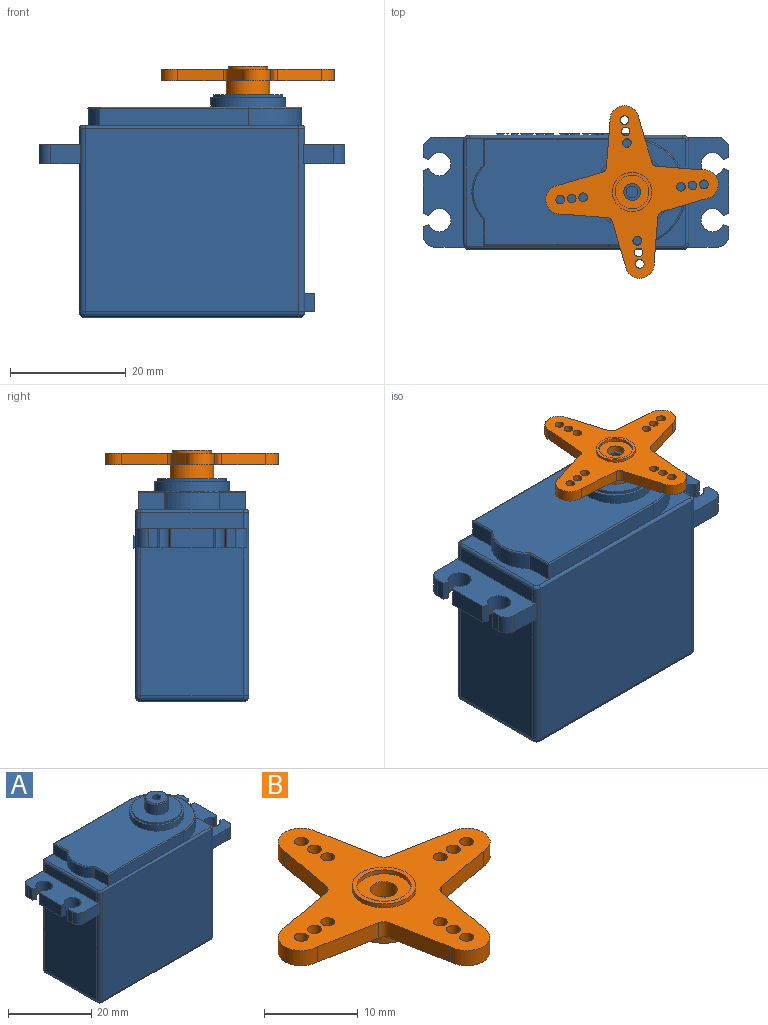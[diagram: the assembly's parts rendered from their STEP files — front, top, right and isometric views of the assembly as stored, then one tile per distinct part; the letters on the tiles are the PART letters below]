
ASSEMBLY  parts=2 mates=1
PART A: 315 faces, bbox 52.9x20.2x41.8 mm
  f0: plane 25.56x17.7mm, normal (1,0,0), area 432.3mm2, adj f18,f38,f39,f40,f310,f311,f313
  f1: plane 37x31.7mm, normal (0,1,0), area 1154.2mm2, adj f40,f45,f46,f67,f85,f86,f87,f88
  f2: plane 38x18.7mm, normal (0,0,1), area 83.6mm2, adj f50,f51,f52,f53,f54,f55,f65,f66
  f3: plane 17.7x2.8mm, normal (1,0,0), area 49.6mm2, adj f17,f38,f40,f71
  f4: plane 17.7x2.8mm, normal (-1,0,0), area 49.6mm2, adj f23,f43,f46,f66
  f5: plane 25.56x17.7mm, normal (-1,0,0), area 452.4mm2, adj f24,f43,f46,f49
  f6: plane 37x17.7mm, normal (0,0,-1), area 654.9mm2, adj f39,f44,f45,f49
  f7: plane 37x31.7mm, normal (0,-1,0), area 1172.9mm2, adj f38,f43,f44,f70
  f8: plane 3.34x1.49mm, normal (1,0,0), area 5mm2, adj f9,f17,f18,f35
  f9: plane 3.34x0.96mm, normal (0.38,0.92,0), area 3.5mm2, adj f8,f10,f17,f18
  f10: cylinder r=2mm len=4mm, axis (0,0,-1), area 36.7mm2, adj f9,f11,f17,f18
  f11: plane 3.34x0.96mm, normal (0.38,-0.92,0), area 3.5mm2, adj f10,f12,f17,f18
  f12: plane 7.38x3.34mm, normal (1,0,0), area 24.6mm2, adj f11,f13,f17,f18
  f13: plane 3.34x0.96mm, normal (0.38,0.92,0), area 3.5mm2, adj f12,f14,f17,f18
  f14: cylinder r=2mm len=4mm, axis (0,0,-1), area 36.7mm2, adj f13,f15,f17,f18
  f15: plane 3.34x0.96mm, normal (0.38,-0.92,0), area 3.5mm2, adj f14,f16,f17,f18
  f16: plane 3.34x1.49mm, normal (1,0,0), area 5mm2, adj f15,f17,f18,f36
  f17: plane 19x7.17mm, normal (0,0,1), area 101.5mm2, adj f3,f8,f9,f10,f11,f12,f13,f14
  f18: plane 19x7.17mm, normal (0,0,-1), area 101.5mm2, adj f0,f8,f9,f10,f11,f12,f13,f14
  f19: plane 5.17x3.34mm, normal (0,1,0), area 17.3mm2, adj f17,f18,f36,f40
  f20: plane 5.17x3.34mm, normal (0,-1,0), area 17.3mm2, adj f17,f18,f35,f38
  f21: plane 5.17x3.34mm, normal (0,-1,0), area 17.3mm2, adj f23,f24,f34,f43
  f22: plane 5.17x3.34mm, normal (0,1,0), area 17.3mm2, adj f23,f24,f37,f46
  f23: plane 19x7.17mm, normal (0,0,1), area 101.5mm2, adj f4,f21,f22,f25,f26,f27,f28,f29
  f24: plane 19x7.17mm, normal (0,0,-1), area 101.5mm2, adj f5,f21,f22,f25,f26,f27,f28,f29
  f25: plane 3.34x0.96mm, normal (-0.38,-0.92,0), area 3.5mm2, adj f23,f24,f26,f33
  f26: cylinder r=2mm len=4mm, axis (0,0,-1), area 36.7mm2, adj f23,f24,f25,f27
  f27: plane 3.34x0.96mm, normal (-0.38,0.92,0), area 3.5mm2, adj f23,f24,f26,f28
  f28: plane 7.38x3.34mm, normal (-1,0,0), area 24.6mm2, adj f23,f24,f27,f29
  f29: plane 3.34x0.96mm, normal (-0.38,-0.92,0), area 3.5mm2, adj f23,f24,f28,f30
  f30: cylinder r=2mm len=4mm, axis (0,0,-1), area 36.7mm2, adj f23,f24,f29,f31
  f31: plane 3.34x0.96mm, normal (-0.38,0.92,0), area 3.5mm2, adj f23,f24,f30,f32
  f32: plane 3.34x1.49mm, normal (-1,0,0), area 5mm2, adj f23,f24,f31,f34
  f33: plane 3.34x1.49mm, normal (-1,0,0), area 5mm2, adj f23,f24,f25,f37
  f34: cylinder r=2mm len=3.34mm, axis (0,0,-1), area 10.5mm2, adj f21,f23,f24,f32
  f35: cylinder r=2mm len=3.34mm, axis (0,0,1), area 10.5mm2, adj f8,f17,f18,f20
  f36: cylinder r=2mm len=3.34mm, axis (0,0,-1), area 10.5mm2, adj f16,f17,f18,f19
  f37: cylinder r=2mm len=3.34mm, axis (0,0,1), area 10.5mm2, adj f22,f23,f24,f33
  f38: cylinder r=1mm len=31.7mm, axis (0,0,-1), area 47.4mm2, adj f0,f3,f7,f17,f18,f20,f41,f72
  f39: cylinder r=1mm len=17.7mm, axis (0,-1,0), area 27.8mm2, adj f0,f6,f41,f42,f312
  f40: cylinder r=1mm len=31.7mm, axis (0,0,1), area 47.4mm2, adj f0,f1,f3,f17,f18,f19,f42,f69
  f41: sphere r=1mm, area 1.6mm2, adj f38,f39,f44
  f42: sphere r=1mm, area 1.6mm2, adj f39,f40,f45
  f43: cylinder r=1mm len=31.7mm, axis (0,0,1), area 47.4mm2, adj f4,f5,f7,f21,f23,f24,f47,f68
  f44: cylinder r=1mm len=37mm, axis (-1,0,0), area 58.1mm2, adj f6,f7,f41,f47
  f45: cylinder r=1mm len=37mm, axis (1,0,0), area 58.1mm2, adj f1,f6,f42,f48
  f46: cylinder r=1mm len=31.7mm, axis (0,0,-1), area 47.4mm2, adj f1,f4,f5,f22,f23,f24,f48,f65
  f47: sphere r=1mm, area 1.6mm2, adj f43,f44,f49
  f48: sphere r=1mm, area 1.6mm2, adj f45,f46,f49
  f49: cylinder r=1mm len=17.7mm, axis (0,1,0), area 27.8mm2, adj f5,f6,f47,f48
  f50: plane 25.7x2.95mm, normal (0,-1,0), area 75.8mm2, adj f2,f51,f55,f61
  f51: cylinder r=9.3mm len=18.6mm, axis (0,0,-1), area 86.2mm2, adj f2,f50,f52,f59
  f52: plane 25.7x2.95mm, normal (0,1,0), area 75.8mm2, adj f2,f51,f53,f60
  f53: plane 4.61x2.95mm, normal (-1,0,0), area 13.6mm2, adj f2,f52,f54,f62
  f54: cylinder r=6.5mm len=9.38mm, axis (0,0,-1), area 30.9mm2, adj f2,f53,f55,f64
  f55: plane 4.61x2.95mm, normal (-1,0,0), area 13.6mm2, adj f2,f50,f54,f63
  f56: plane 36.5x18.1mm, normal (0,0,1), area 469.2mm2, adj f57,f59,f60,f61,f62,f63,f64
  f57: cylinder r=6.5mm len=13mm, axis (0,0,-1), area 66.2mm2, adj f56,f58
  f58: plane 13x13mm, normal (0,0,1), area 19.6mm2, adj f57,f73
  f59: torus R=9.05mm, axis (0,0,1), area 11.4mm2, adj f51,f56,f60,f61
  f60: cylinder r=0.25mm len=25.7mm, axis (1,0,0), area 10.1mm2, adj f52,f56,f59,f62
  f61: cylinder r=0.25mm len=25.7mm, axis (-1,0,0), area 10.1mm2, adj f50,f56,f59,f63
  f62: cylinder r=0.25mm len=4.72mm, axis (0,1,0), area 1.8mm2, adj f53,f56,f60,f64
  f63: cylinder r=0.25mm len=4.72mm, axis (0,1,0), area 1.8mm2, adj f55,f56,f61,f64
  f64: torus R=6.25mm, axis (0,0,1), area 4.1mm2, adj f54,f56,f62,f63
  f65: torus R=0.5mm, axis (0,0,1), area 1mm2, adj f2,f46,f66,f67
  f66: cylinder r=0.5mm len=17.7mm, axis (0,-1,0), area 13.9mm2, adj f2,f4,f65,f68
  f67: cylinder r=0.5mm len=37mm, axis (-1,0,0), area 29.1mm2, adj f1,f2,f65,f69
  f68: torus R=0.5mm, axis (0,0,1), area 1mm2, adj f2,f43,f66,f70
  f69: torus R=0.5mm, axis (0,0,1), area 1mm2, adj f2,f40,f67,f71
  f70: cylinder r=0.5mm len=37mm, axis (1,0,0), area 29.1mm2, adj f2,f7,f68,f72
  f71: cylinder r=0.5mm len=17.7mm, axis (0,1,0), area 13.9mm2, adj f2,f3,f69,f72
  f72: torus R=0.5mm, axis (0,0,1), area 1mm2, adj f2,f38,f70,f71
  f73: cylinder r=6mm len=12mm, axis (0,0,-1), area 18.8mm2, adj f58,f74
  f74: plane 12x12mm, normal (0,0,1), area 88mm2, adj f73,f76
  f75: cylinder r=1mm len=3.25mm, axis (0,0,-1), area 20.4mm2, adj f77,f78
  f76: cylinder r=2.82mm len=5.65mm, axis (0,0,-1), area 53.2mm2, adj f74,f309
  f77: plane 5.15x5.15mm, normal (0,0,1), area 17.7mm2, adj f75,f309
  f78: plane 2x2mm, normal (0,0,1), area 3.1mm2, adj f75
  f79: plane 0.25x0.22mm, normal (0,0,1), area 0.1mm2, adj f80,f93,f94,f95
  f80: plane 0.84x0.25mm, normal (-1,0,0), area 0.2mm2, adj f79,f81,f94,f95
  f81: plane 0.27x0.25mm, normal (0,0,-1), area 0.1mm2, adj f80,f82,f94,f95
  f82: extruded ~0.42x0.25mm, area 0.1mm2, adj f81,f83,f94,f95
  f83: extruded ~0.31x0.25mm, area 0.1mm2, adj f82,f84,f94,f95
  f84: extruded ~0.33x0.25mm, area 0.1mm2, adj f83,f93,f94,f95
  f85: extruded ~0.49x0.25mm, area 0.1mm2, adj f1,f86,f92,f94
  f86: extruded ~0.78x0.61mm, area 0.3mm2, adj f1,f85,f87,f94
  f87: plane 0.54x0.25mm, normal (0,0,1), area 0.1mm2, adj f1,f86,f88,f94
  f88: plane 2.08x0.25mm, normal (1,0,0), area 0.5mm2, adj f1,f87,f89,f94
  f89: plane 0.25x0.24mm, normal (0,0,-1), area 0.1mm2, adj f1,f88,f90,f94
  f90: plane 0.82x0.25mm, normal (-1,0,0), area 0.2mm2, adj f1,f89,f91,f94
  f91: plane 0.25x0.24mm, normal (0,0,-1), area 0.1mm2, adj f1,f90,f92,f94
  f92: extruded ~0.62x0.25mm, area 0.2mm2, adj f1,f85,f91,f94
  f93: extruded ~0.46x0.25mm, area 0.1mm2, adj f79,f84,f94,f95
  f94: plane 2.08x1.32mm, normal (0,1,0), area 1.1mm2, adj f79,f80,f81,f82,f83,f84,f85,f86
  f95: plane 0.84x0.83mm, normal (0,1,0), area 0.6mm2, adj f79,f80,f81,f82,f83,f84,f93
  f96: plane 0.64x0.25mm, normal (0.94,0,-0.35), area 0.2mm2, adj f97,f108,f109,f110
  f97: plane 0.67x0.25mm, normal (0,0,1), area 0.2mm2, adj f96,f98,f109,f110
  f98: plane 0.64x0.25mm, normal (-0.94,0,-0.35), area 0.2mm2, adj f97,f99,f109,f110
  f99: extruded ~0.3x0.25mm, area 0.1mm2, adj f98,f108,f109,f110
  f100: plane 0.66x0.26mm, normal (0.93,0,-0.36), area 0.2mm2, adj f1,f101,f107,f109
  f101: plane 0.25x0.25mm, normal (0,0,-1), area 0.1mm2, adj f1,f100,f102,f109
  f102: plane 2.09x0.82mm, normal (-0.93,0,0.36), area 0.6mm2, adj f1,f101,f103,f109
  f103: plane 0.25x0.2mm, normal (0,0,1), area 0.1mm2, adj f1,f102,f104,f109
  f104: plane 2.09x0.82mm, normal (0.93,0,0.37), area 0.6mm2, adj f1,f103,f105,f109
  f105: plane 0.25x0.24mm, normal (0,0,-1), area 0.1mm2, adj f1,f104,f106,f109
  f106: plane 0.66x0.26mm, normal (-0.93,0,-0.36), area 0.2mm2, adj f1,f105,f107,f109
  f107: plane 0.83x0.25mm, normal (0,0,-1), area 0.2mm2, adj f1,f100,f106,f109
  f108: extruded ~0.3x0.25mm, area 0.1mm2, adj f96,f99,f109,f110
  f109: plane 2.09x1.84mm, normal (0,1,0), area 1.1mm2, adj f96,f97,f98,f99,f100,f101,f102,f103
  f110: plane 0.94x0.67mm, normal (0,1,0), area 0.3mm2, adj f96,f97,f98,f99,f108
  f111: plane 0.33x0.25mm, normal (0,0,1), area 0.1mm2, adj f112,f128,f129,f130
  f112: plane 0.79x0.25mm, normal (-1,0,0), area 0.2mm2, adj f111,f113,f129,f130
  f113: plane 0.31x0.25mm, normal (0,0,-1), area 0.1mm2, adj f112,f114,f129,f130
  f114: extruded ~0.39x0.25mm, area 0.1mm2, adj f113,f115,f129,f130
  f115: extruded ~0.3x0.25mm, area 0.1mm2, adj f114,f116,f129,f130
  f116: extruded ~0.31x0.25mm, area 0.1mm2, adj f115,f128,f129,f130
  f117: plane 0.86x0.25mm, normal (-1,0,0), area 0.2mm2, adj f1,f118,f127,f129
  f118: plane 0.43x0.25mm, normal (0,0,-1), area 0.1mm2, adj f1,f117,f119,f129
  f119: plane 0.86x0.5mm, normal (0.86,0,-0.5), area 0.3mm2, adj f1,f118,f120,f129
  f120: plane 0.29x0.25mm, normal (0,0,-1), area 0.1mm2, adj f1,f119,f121,f129
  f121: plane 0.93x0.56mm, normal (-0.86,0,0.52), area 0.3mm2, adj f1,f120,f122,f129
  f122: extruded ~0.56x0.42mm, area 0.2mm2, adj f1,f121,f123,f129
  f123: extruded ~0.44x0.25mm, area 0.1mm2, adj f1,f122,f124,f129
  f124: extruded ~0.57x0.25mm, area 0.1mm2, adj f1,f123,f125,f129
  f125: plane 0.57x0.25mm, normal (0,0,1), area 0.1mm2, adj f1,f124,f126,f129
  f126: plane 2.08x0.25mm, normal (1,0,0), area 0.5mm2, adj f1,f125,f127,f129
  f127: plane 0.25x0.24mm, normal (0,0,-1), area 0.1mm2, adj f1,f117,f126,f129
  f128: extruded ~0.38x0.25mm, area 0.1mm2, adj f111,f116,f129,f130
  f129: plane 2.08x1.46mm, normal (0,1,0), area 1.3mm2, adj f111,f112,f113,f114,f115,f116,f117,f118
  f130: plane 0.83x0.79mm, normal (0,1,0), area 0.6mm2, adj f111,f112,f113,f114,f115,f116,f128
  f131: plane 0.26x0.25mm, normal (0,0,1), area 0.1mm2, adj f1,f132,f139,f140
  f132: plane 1.34x0.48mm, normal (0.94,0,0.33), area 0.4mm2, adj f1,f131,f133,f140
  f133: extruded ~0.46x0.25mm, area 0.1mm2, adj f1,f132,f134,f140
  f134: extruded ~0.45x0.25mm, area 0.1mm2, adj f1,f133,f135,f140
  f135: plane 1.34x0.48mm, normal (-0.94,0,0.33), area 0.4mm2, adj f1,f134,f136,f140
  f136: plane 0.26x0.25mm, normal (0,0,1), area 0.1mm2, adj f1,f135,f137,f140
  f137: plane 2.08x0.75mm, normal (0.94,0,-0.34), area 0.6mm2, adj f1,f136,f138,f140
  f138: plane 0.25x0.24mm, normal (0,0,-1), area 0.1mm2, adj f1,f137,f139,f140
  f139: plane 2.08x0.75mm, normal (-0.94,0,-0.34), area 0.6mm2, adj f1,f131,f138,f140
  f140: plane 2.08x1.73mm, normal (0,1,0), area 1mm2, adj f131,f132,f133,f134,f135,f136,f137,f138
  f141: plane 1.16x0.25mm, normal (0,0,-1), area 0.3mm2, adj f1,f142,f152,f153
  f142: plane 0.25x0.22mm, normal (-1,0,0), area 0.1mm2, adj f1,f141,f143,f153
  f143: plane 0.92x0.25mm, normal (0,0,1), area 0.2mm2, adj f1,f142,f144,f153
  f144: plane 0.76x0.25mm, normal (-1,0,0), area 0.2mm2, adj f1,f143,f145,f153
  f145: plane 0.86x0.25mm, normal (0,0,-1), area 0.2mm2, adj f1,f144,f146,f153
  f146: plane 0.25x0.21mm, normal (-1,0,0), area 0.1mm2, adj f1,f145,f147,f153
  f147: plane 0.86x0.25mm, normal (0,0,1), area 0.2mm2, adj f1,f146,f148,f153
  f148: plane 0.67x0.25mm, normal (-1,0,0), area 0.2mm2, adj f1,f147,f149,f153
  f149: plane 0.92x0.25mm, normal (0,0,-1), area 0.2mm2, adj f1,f148,f150,f153
  f150: plane 0.25x0.21mm, normal (-1,0,0), area 0.1mm2, adj f1,f149,f151,f153
  f151: plane 1.16x0.25mm, normal (0,0,1), area 0.3mm2, adj f1,f150,f152,f153
  f152: plane 2.08x0.25mm, normal (1,0,0), area 0.5mm2, adj f1,f141,f151,f153
  f153: plane 2.08x1.16mm, normal (0,1,0), area 1.1mm2, adj f141,f142,f143,f144,f145,f146,f147,f148
  f154: extruded ~0.61x0.25mm, area 0.2mm2, adj f155,f167,f168,f169
  f155: extruded ~0.63x0.25mm, area 0.2mm2, adj f154,f156,f168,f169
  f156: extruded ~0.65x0.25mm, area 0.2mm2, adj f155,f157,f168,f169
  f157: plane 0.29x0.25mm, normal (0,0,1), area 0.1mm2, adj f156,f158,f168,f169
  f158: plane 1.66x0.25mm, normal (-1,0,0), area 0.4mm2, adj f157,f159,f168,f169
  f159: plane 0.35x0.25mm, normal (0,0,-1), area 0.1mm2, adj f158,f167,f168,f169
  f160: extruded ~0.79x0.28mm, area 0.2mm2, adj f1,f161,f166,f168
  f161: extruded ~0.75x0.27mm, area 0.2mm2, adj f1,f160,f162,f168
  f162: extruded ~0.75x0.27mm, area 0.2mm2, adj f1,f161,f163,f168
  f163: plane 0.64x0.25mm, normal (0,0,1), area 0.2mm2, adj f1,f162,f164,f168
  f164: plane 2.08x0.25mm, normal (1,0,0), area 0.5mm2, adj f1,f163,f165,f168
  f165: plane 0.58x0.25mm, normal (0,0,-1), area 0.1mm2, adj f1,f164,f166,f168
  f166: extruded ~0.8x0.27mm, area 0.2mm2, adj f1,f160,f165,f168
  f167: extruded ~0.61x0.25mm, area 0.2mm2, adj f154,f159,f168,f169
  f168: plane 2.08x1.66mm, normal (0,1,0), area 1.4mm2, adj f154,f155,f156,f157,f158,f159,f160,f161
  f169: plane 1.66x1.16mm, normal (0,1,0), area 1.7mm2, adj f154,f155,f156,f157,f158,f159,f167
  f170: plane 1.04x0.55mm, normal (0.88,0,0.47), area 0.3mm2, adj f1,f171,f178,f179
  f171: plane 1.04x0.55mm, normal (-0.88,0,0.47), area 0.3mm2, adj f1,f170,f172,f179
  f172: plane 0.26x0.25mm, normal (0,0,1), area 0.1mm2, adj f1,f171,f173,f179
  f173: plane 1.28x0.69mm, normal (0.88,0,-0.47), area 0.4mm2, adj f1,f172,f174,f179
  f174: plane 0.79x0.25mm, normal (1,0,0), area 0.2mm2, adj f1,f173,f175,f179
  f175: plane 0.25x0.24mm, normal (0,0,-1), area 0.1mm2, adj f1,f174,f176,f179
  f176: plane 0.81x0.25mm, normal (-1,0,0), area 0.2mm2, adj f1,f175,f177,f179
  f177: plane 1.27x0.69mm, normal (-0.88,0,-0.48), area 0.4mm2, adj f1,f176,f178,f179
  f178: plane 0.26x0.25mm, normal (0,0,1), area 0.1mm2, adj f1,f170,f177,f179
  f179: plane 2.08x1.63mm, normal (0,1,0), area 0.8mm2, adj f170,f171,f172,f173,f174,f175,f176,f177
  f180: plane 0.33x0.25mm, normal (0,0,1), area 0.1mm2, adj f181,f197,f198,f199
  f181: plane 0.79x0.25mm, normal (-1,0,0), area 0.2mm2, adj f180,f182,f198,f199
  f182: plane 0.31x0.25mm, normal (0,0,-1), area 0.1mm2, adj f181,f183,f198,f199
  f183: extruded ~0.39x0.25mm, area 0.1mm2, adj f182,f184,f198,f199
  f184: extruded ~0.3x0.25mm, area 0.1mm2, adj f183,f185,f198,f199
  f185: extruded ~0.31x0.25mm, area 0.1mm2, adj f184,f197,f198,f199
  f186: plane 0.86x0.25mm, normal (-1,0,0), area 0.2mm2, adj f1,f187,f196,f198
  f187: plane 0.43x0.25mm, normal (0,0,-1), area 0.1mm2, adj f1,f186,f188,f198
  f188: plane 0.86x0.5mm, normal (0.86,0,-0.5), area 0.3mm2, adj f1,f187,f189,f198
  f189: plane 0.29x0.25mm, normal (0,0,-1), area 0.1mm2, adj f1,f188,f190,f198
  f190: plane 0.93x0.56mm, normal (-0.86,0,0.52), area 0.3mm2, adj f1,f189,f191,f198
  f191: extruded ~0.56x0.42mm, area 0.2mm2, adj f1,f190,f192,f198
  f192: extruded ~0.44x0.25mm, area 0.1mm2, adj f1,f191,f193,f198
  f193: extruded ~0.57x0.25mm, area 0.1mm2, adj f1,f192,f194,f198
  f194: plane 0.57x0.25mm, normal (0,0,1), area 0.1mm2, adj f1,f193,f195,f198
  f195: plane 2.08x0.25mm, normal (1,0,0), area 0.5mm2, adj f1,f194,f196,f198
  f196: plane 0.25x0.24mm, normal (0,0,-1), area 0.1mm2, adj f1,f186,f195,f198
  f197: extruded ~0.38x0.25mm, area 0.1mm2, adj f180,f185,f198,f199
  f198: plane 2.08x1.46mm, normal (0,1,0), area 1.3mm2, adj f180,f181,f182,f183,f184,f185,f186,f187
  f199: plane 0.83x0.79mm, normal (0,1,0), area 0.6mm2, adj f180,f181,f182,f183,f184,f185,f197
  f200: extruded ~0.46x0.25mm, area 0.1mm2, adj f201,f216,f217,f218
  f201: extruded ~0.45x0.25mm, area 0.1mm2, adj f200,f202,f217,f218
  f202: extruded ~0.35x0.25mm, area 0.1mm2, adj f201,f203,f217,f218
  f203: extruded ~0.36x0.25mm, area 0.1mm2, adj f202,f204,f217,f218
  f204: extruded ~0.45x0.25mm, area 0.1mm2, adj f203,f205,f217,f218
  f205: extruded ~0.46x0.25mm, area 0.1mm2, adj f204,f206,f217,f218
  f206: extruded ~0.35x0.25mm, area 0.1mm2, adj f205,f216,f217,f218
  f207: extruded ~0.6x0.25mm, area 0.2mm2, adj f1,f208,f215,f217
  f208: extruded ~0.59x0.25mm, area 0.2mm2, adj f1,f207,f209,f217
  f209: extruded ~0.52x0.25mm, area 0.1mm2, adj f1,f208,f210,f217
  f210: extruded ~0.53x0.25mm, area 0.1mm2, adj f1,f209,f211,f217
  f211: extruded ~0.59x0.25mm, area 0.2mm2, adj f1,f210,f212,f217
  f212: extruded ~0.43x0.25mm, area 0.1mm2, adj f1,f211,f213,f217
  f213: extruded ~0.28x0.25mm, area 0.1mm2, adj f1,f212,f214,f217
  f214: extruded ~0.37x0.25mm, area 0.1mm2, adj f1,f213,f215,f217
  f215: extruded ~0.53x0.25mm, area 0.1mm2, adj f1,f207,f214,f217
  f216: extruded ~0.35x0.25mm, area 0.1mm2, adj f200,f206,f217,f218
  f217: plane 1.62x1.43mm, normal (0,1,0), area 0.9mm2, adj f200,f201,f202,f203,f204,f205,f206,f207
  f218: plane 1.22x0.94mm, normal (0,1,0), area 1mm2, adj f200,f201,f202,f203,f204,f205,f206,f216
  f219: plane 1.01x0.25mm, normal (1,0,0), area 0.3mm2, adj f1,f220,f246,f247
  f220: plane 0.25x0.24mm, normal (0,0,-1), area 0.1mm2, adj f1,f219,f221,f247
  f221: plane 1.02x0.25mm, normal (-1,0,0), area 0.3mm2, adj f1,f220,f222,f247
  f222: extruded ~0.43x0.25mm, area 0.1mm2, adj f1,f221,f223,f247
  f223: extruded ~0.4x0.25mm, area 0.1mm2, adj f1,f222,f224,f247
  f224: extruded ~0.3x0.25mm, area 0.1mm2, adj f1,f223,f225,f247
  f225: extruded ~0.25x0.2mm, area 0.1mm2, adj f1,f224,f226,f247
  f226: plane 0.25x0.01mm, normal (0,0,1), area 0mm2, adj f1,f225,f227,f247
  f227: extruded ~0.48x0.26mm, area 0.1mm2, adj f1,f226,f228,f247
  f228: extruded ~0.27x0.25mm, area 0.1mm2, adj f1,f227,f229,f247
  f229: extruded ~0.25x0.19mm, area 0.1mm2, adj f1,f228,f230,f247
  f230: plane 0.25x0.01mm, normal (0,0,1), area 0mm2, adj f1,f229,f231,f247
  f231: plane 0.25x0.21mm, normal (-0.98,0,0.18), area 0.1mm2, adj f1,f230,f232,f247
  f232: plane 0.25x0.19mm, normal (0,0,1), area 0mm2, adj f1,f231,f233,f247
  f233: plane 1.56x0.25mm, normal (1,0,0), area 0.4mm2, adj f1,f232,f234,f247
  f234: plane 0.25x0.24mm, normal (0,0,-1), area 0.1mm2, adj f1,f233,f235,f247
  f235: plane 0.82x0.25mm, normal (-1,0,0), area 0.2mm2, adj f1,f234,f236,f247
  f236: extruded ~0.44x0.25mm, area 0.1mm2, adj f1,f235,f237,f247
  f237: extruded ~0.32x0.25mm, area 0.1mm2, adj f1,f236,f238,f247
  f238: extruded ~0.25x0.25mm, area 0.1mm2, adj f1,f237,f239,f247
  f239: extruded ~0.28x0.25mm, area 0.1mm2, adj f1,f238,f240,f247
  f240: plane 1.01x0.25mm, normal (1,0,0), area 0.3mm2, adj f1,f239,f241,f247
  f241: plane 0.25x0.24mm, normal (0,0,-1), area 0.1mm2, adj f1,f240,f242,f247
  f242: plane 0.87x0.25mm, normal (-1,0,0), area 0.2mm2, adj f1,f241,f243,f247
  f243: extruded ~0.39x0.25mm, area 0.1mm2, adj f1,f242,f244,f247
  f244: extruded ~0.33x0.25mm, area 0.1mm2, adj f1,f243,f245,f247
  f245: extruded ~0.25x0.25mm, area 0.1mm2, adj f1,f244,f246,f247
  f246: extruded ~0.28x0.25mm, area 0.1mm2, adj f1,f219,f245,f247
  f247: plane 2.22x1.59mm, normal (0,1,0), area 1.4mm2, adj f219,f220,f221,f222,f223,f224,f225,f226
  f248: extruded ~0.35x0.25mm, area 0.1mm2, adj f249,f274,f275,f276
  f249: extruded ~0.25x0.22mm, area 0.1mm2, adj f248,f250,f275,f276
  f250: extruded ~0.25x0.2mm, area 0.1mm2, adj f249,f251,f275,f276
  f251: extruded ~0.25x0.24mm, area 0.1mm2, adj f250,f252,f275,f276
  f252: extruded ~0.41x0.25mm, area 0.1mm2, adj f251,f253,f275,f276
  f253: plane 0.25x0.24mm, normal (-0.04,0,-1), area 0.1mm2, adj f252,f254,f275,f276
  f254: plane 0.25x0.14mm, normal (1,0,0), area 0mm2, adj f253,f274,f275,f276
  f255: plane 0.25x0.22mm, normal (0.98,0,-0.21), area 0.1mm2, adj f1,f256,f273,f275
  f256: plane 0.25x0.18mm, normal (0,0,-1), area 0mm2, adj f1,f255,f257,f275
  f257: plane 1.06x0.25mm, normal (-1,0,0), area 0.3mm2, adj f1,f256,f258,f275
  f258: extruded ~0.4x0.25mm, area 0.1mm2, adj f1,f257,f259,f275
  f259: extruded ~0.41x0.25mm, area 0.1mm2, adj f1,f258,f260,f275
  f260: extruded ~0.28x0.25mm, area 0.1mm2, adj f1,f259,f261,f275
  f261: extruded ~0.25x0.25mm, area 0.1mm2, adj f1,f260,f262,f275
  f262: plane 0.25x0.18mm, normal (0.93,0,-0.37), area 0mm2, adj f1,f261,f263,f275
  f263: extruded ~0.44x0.25mm, area 0.1mm2, adj f1,f262,f264,f275
  f264: extruded ~0.25x0.25mm, area 0.1mm2, adj f1,f263,f265,f275
  f265: extruded ~0.27x0.25mm, area 0.1mm2, adj f1,f264,f266,f275
  f266: plane 0.25x0.1mm, normal (1,0,0), area 0mm2, adj f1,f265,f267,f275
  f267: plane 0.26x0.25mm, normal (0.03,0,1), area 0.1mm2, adj f1,f266,f268,f275
  f268: extruded ~0.75x0.49mm, area 0.3mm2, adj f1,f267,f269,f275
  f269: extruded ~0.34x0.25mm, area 0.1mm2, adj f1,f268,f270,f275
  f270: extruded ~0.36x0.25mm, area 0.1mm2, adj f1,f269,f271,f275
  f271: extruded ~0.29x0.25mm, area 0.1mm2, adj f1,f270,f272,f275
  f272: extruded ~0.25x0.23mm, area 0.1mm2, adj f1,f271,f273,f275
  f273: plane 0.25x0.01mm, normal (0,0,-1), area 0mm2, adj f1,f255,f272,f275
  f274: extruded ~0.34x0.25mm, area 0.1mm2, adj f248,f254,f275,f276
  f275: plane 1.61x1.25mm, normal (0,1,0), area 1mm2, adj f248,f249,f250,f251,f252,f253,f254,f255
  f276: plane 0.77x0.6mm, normal (0,1,0), area 0.4mm2, adj f248,f249,f250,f251,f252,f253,f254,f274
  f277: plane 0.25x0.24mm, normal (0,0,-1), area 0.1mm2, adj f1,f278,f280,f281
  f278: plane 1.56x0.25mm, normal (-1,0,0), area 0.4mm2, adj f1,f277,f279,f281
  f279: plane 0.25x0.24mm, normal (0,0,1), area 0.1mm2, adj f1,f278,f280,f281
  f280: plane 1.56x0.25mm, normal (1,0,0), area 0.4mm2, adj f1,f277,f279,f281
  f281: plane 1.56x0.24mm, normal (0,1,0), area 0.4mm2, adj f277,f278,f279,f280
  f282: extruded ~0.25x0.12mm, area 0mm2, adj f1,f283,f289,f290
  f283: extruded ~0.25x0.12mm, area 0mm2, adj f1,f282,f284,f290
  f284: extruded ~0.25x0.1mm, area 0mm2, adj f1,f283,f285,f290
  f285: extruded ~0.25x0.1mm, area 0mm2, adj f1,f284,f286,f290
  f286: extruded ~0.25x0.12mm, area 0mm2, adj f1,f285,f287,f290
  f287: extruded ~0.25x0.12mm, area 0mm2, adj f1,f286,f288,f290
  f288: extruded ~0.25x0.1mm, area 0mm2, adj f1,f287,f289,f290
  f289: extruded ~0.25x0.1mm, area 0mm2, adj f1,f282,f288,f290
  f290: plane 0.31x0.28mm, normal (0,1,0), area 0.1mm2, adj f282,f283,f284,f285,f286,f287,f288,f289
  f291: plane 1.01x0.25mm, normal (1,0,0), area 0.3mm2, adj f1,f292,f307,f308
  f292: plane 0.25x0.24mm, normal (0,0,-1), area 0.1mm2, adj f1,f291,f293,f308
  f293: plane 1.02x0.25mm, normal (-1,0,0), area 0.3mm2, adj f1,f292,f294,f308
  f294: extruded ~0.43x0.25mm, area 0.1mm2, adj f1,f293,f295,f308
  f295: extruded ~0.42x0.25mm, area 0.1mm2, adj f1,f294,f296,f308
  f296: extruded ~0.29x0.25mm, area 0.1mm2, adj f1,f295,f297,f308
  f297: extruded ~0.25x0.2mm, area 0.1mm2, adj f1,f296,f298,f308
  f298: plane 0.25x0.01mm, normal (0,0,1), area 0mm2, adj f1,f297,f299,f308
  f299: plane 0.25x0.21mm, normal (-0.98,0,0.18), area 0.1mm2, adj f1,f298,f300,f308
  f300: plane 0.25x0.19mm, normal (0,0,1), area 0mm2, adj f1,f299,f301,f308
  f301: plane 1.56x0.25mm, normal (1,0,0), area 0.4mm2, adj f1,f300,f302,f308
  f302: plane 0.25x0.24mm, normal (0,0,-1), area 0.1mm2, adj f1,f301,f303,f308
  f303: plane 0.82x0.25mm, normal (-1,0,0), area 0.2mm2, adj f1,f302,f304,f308
  f304: extruded ~0.44x0.25mm, area 0.1mm2, adj f1,f303,f305,f308
  f305: extruded ~0.36x0.25mm, area 0.1mm2, adj f1,f304,f306,f308
  f306: extruded ~0.27x0.25mm, area 0.1mm2, adj f1,f305,f307,f308
  f307: extruded ~0.28x0.25mm, area 0.1mm2, adj f1,f291,f306,f308
  f308: plane 1.59x1.3mm, normal (0,1,0), area 0.9mm2, adj f291,f292,f293,f294,f295,f296,f297,f298
  f309: cone r=2.58mm half-angle=45deg, axis (0,0,-1), area 6mm2, adj f76,f77
  f310: plane 6.4x1.75mm, normal (0,0,1), area 11.2mm2, adj f0,f311,f313,f314
  f311: plane 3.15x1.75mm, normal (0,-1,0), area 5.5mm2, adj f0,f310,f312,f314
  f312: plane 6.4x1.75mm, normal (0,0,-1), area 11.2mm2, adj f39,f311,f313,f314
  f313: plane 3.15x1.75mm, normal (0,1,0), area 5.5mm2, adj f0,f310,f312,f314
  f314: plane 6.4x3.15mm, normal (1,0,0), area 20.2mm2, adj f310,f311,f312,f313
PART B: 39 faces, bbox 30x30x4.9 mm
  f0: plane 5.9x5.9mm, normal (0,0,-1), area 20.7mm2, adj f35,f36
  f1: cylinder r=2.5mm len=5mm, axis (0,0,-1), area 15.7mm2, adj f2,f27,f29,f30
  f2: plane 7.75x2mm, normal (-0.98,0.18,0), area 15.8mm2, adj f1,f3,f29,f30
  f3: cylinder r=1mm len=2mm, axis (0,0,-1), area 2.4mm2, adj f2,f4,f29,f30
  f4: plane 7.75x2mm, normal (-0.18,0.98,0), area 15.8mm2, adj f3,f5,f29,f30
  f5: cylinder r=2.5mm len=5mm, axis (0,0,-1), area 15.7mm2, adj f4,f6,f29,f30
  f6: plane 7.75x2mm, normal (-0.18,-0.98,0), area 15.8mm2, adj f5,f7,f29,f30
  f7: cylinder r=1mm len=2mm, axis (0,0,-1), area 2.4mm2, adj f6,f8,f29,f30
  f8: plane 7.75x2mm, normal (-0.98,-0.18,0), area 15.8mm2, adj f7,f9,f29,f30
  f9: cylinder r=2.5mm len=5mm, axis (0,0,-1), area 15.7mm2, adj f8,f10,f29,f30
  f10: plane 7.75x2mm, normal (0.98,-0.18,0), area 15.8mm2, adj f9,f11,f29,f30
  f11: cylinder r=1mm len=2mm, axis (0,0,-1), area 2.4mm2, adj f10,f12,f29,f30
  f12: plane 7.75x2mm, normal (0.18,-0.98,0), area 15.8mm2, adj f11,f13,f29,f30
  f13: cylinder r=2.5mm len=5mm, axis (0,0,-1), area 15.7mm2, adj f12,f14,f29,f30
  f14: plane 7.75x2mm, normal (0.18,0.98,0), area 15.8mm2, adj f13,f15,f29,f30
  f15: cylinder r=1mm len=2mm, axis (0,0,-1), area 2.4mm2, adj f14,f27,f29,f30
  f16: cylinder r=0.75mm len=2mm, axis (0,0,-1), area 9.4mm2, adj f29,f30
  f17: cylinder r=0.75mm len=2mm, axis (0,0,-1), area 9.4mm2, adj f29,f30
  f18: cylinder r=0.75mm len=2mm, axis (0,0,-1), area 9.4mm2, adj f29,f30
  f19: cylinder r=0.75mm len=2mm, axis (0,0,-1), area 9.4mm2, adj f29,f30
  f20: cylinder r=0.75mm len=2mm, axis (0,0,-1), area 9.4mm2, adj f29,f30
  f21: cylinder r=0.75mm len=2mm, axis (0,0,-1), area 9.4mm2, adj f29,f30
  f22: cylinder r=0.75mm len=2mm, axis (0,0,-1), area 9.4mm2, adj f29,f30
  f23: cylinder r=0.75mm len=2mm, axis (0,0,-1), area 9.4mm2, adj f29,f30
  f24: cylinder r=0.75mm len=2mm, axis (0,0,-1), area 9.4mm2, adj f29,f30
  f25: cylinder r=0.75mm len=2mm, axis (0,0,-1), area 9.4mm2, adj f29,f30
  f26: cylinder r=0.75mm len=2mm, axis (0,0,-1), area 9.4mm2, adj f29,f30
  f27: plane 7.75x2mm, normal (0.98,0.18,0), area 15.8mm2, adj f1,f15,f29,f30
  f28: cylinder r=0.75mm len=2mm, axis (0,0,-1), area 9.4mm2, adj f29,f30
  f29: plane 30x30mm, normal (0,0,1), area 270.4mm2, adj f1,f2,f3,f4,f5,f6,f7,f8
  f30: plane 30x30mm, normal (0,0,-1), area 262.3mm2, adj f1,f2,f3,f4,f5,f6,f7,f8
  f31: cylinder r=2.9mm len=5.8mm, axis (0,0,-1), area 9.1mm2, adj f33,f34
  f32: cylinder r=3.4mm len=6.8mm, axis (0,0,-1), area 10.7mm2, adj f29,f33
  f33: plane 6.8x6.8mm, normal (0,0,1), area 9.9mm2, adj f31,f32
  f34: plane 5.8x5.8mm, normal (0,0,1), area 19.8mm2, adj f31,f35
  f35: cylinder r=1.45mm len=2.9mm, axis (0,0,1), area 18.2mm2, adj f0,f34
  f36: cylinder r=2.95mm len=5.9mm, axis (0,0,1), area 44.5mm2, adj f0,f38
  f37: cylinder r=3.76mm len=7.52mm, axis (0,0,1), area 56.7mm2, adj f30,f38
  f38: plane 7.52x7.52mm, normal (0,0,-1), area 17.1mm2, adj f36,f37
PLACE A at identity fixed
PLACE B rot(axis=(0,0,-1),173.9deg) t=(0,0,14.36)mm
MATE revolute B.f36 <-> A.f76  axis (0,0,-1) through (0,0,11.96)mm
